# Revit family: Холодильник
name_source: partatom
category: Оборудование
revit_build: Autodesk Revit 2017 (Build: 20170118_1100(x64)
units: mm (PartAtom-declared; Revit-internal decimal feet)

## family parameters
Всегда вертикально = Да
На основе рабочей плоскости = Нет
Общий = Нет
При загрузке вырезать с полостями = Нет
Размер круглого соединителя = Использовать диаметр
Тип детали = Нормальный
Точка расчета площади = Нет

## types (4) — shared parameters
Группа модели = ТХ
Изготовитель = Severin
Общ_Единицы измерения = шт.
Общ_Задание = ЭМ
Общ_Напряжение = 220 В

## per-type parameters (varying)
| type | Общ_Высота | Общ_Глубина | Общ_Масса | Общ_Мощность номинальная | Общ_Наименование | Общ_Позиция | Общ_Поставщик | Общ_Тип, марка | Общ_Ширина |
| Для миникухни | 630 мм | 510 мм | 16 | 200 Вт | Холодильник, объём холодильно камеры 69 л |  | SUPRA | RF-075 | 445 мм |
| Без морозилки | 1450 мм | 625 мм | 53 | 100 Вт | Холодильник, объём холодильно камеры 275 л |  | Бирюса | 542 | 600 мм |
| Бирюса R108CA 480х605х865 | 1450 мм | 625 мм | 53 | 100 Вт | Холодильник, объём холодильно камеры 275 л | 97 | Бирюса | 542 | 600 мм |
| ХФ-140 | 910 мм | 610 мм | 40 | 150 Вт | Холодильник фармацевтический, объём холодильной камеры 140 л |  | Позис | ХФ-140 | 600 мм |
